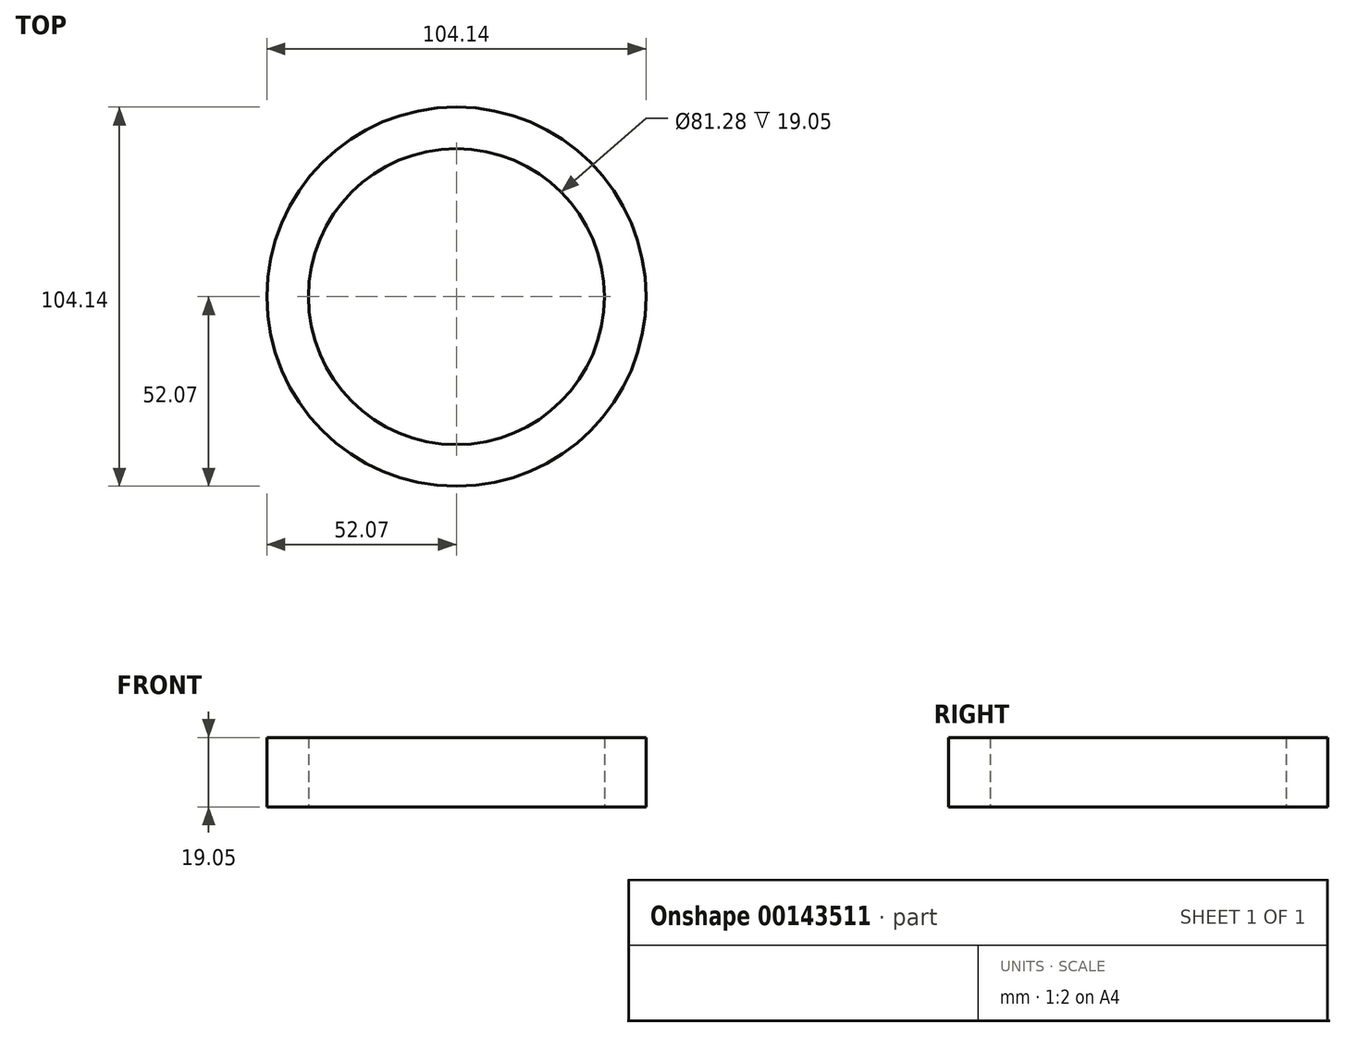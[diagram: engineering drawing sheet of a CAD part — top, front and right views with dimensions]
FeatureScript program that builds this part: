
annotation { "Feature Type Name" : "Feature", "Feature Type Description" : "" }
export const myFeature = defineFeature(function(context is Context, id is Id, definition is map)
    precondition{}
    {
        {
            var Q0;
            Q0=qCreatedBy(makeId("Top.planeOp"),FACE);
            var sketch = newSketch(context, id + "F0", { "sketchPlane" : qUnion([Q0])});
            skCircle(sketch, "E0", {"center": v(0, 0) * mm, "radius": 40.64 * mm});
            skSolve(sketch);
        }
        {
            var Q0;
            Q0=qCreatedBy(makeId("Top.planeOp"),FACE);
            var sketch = newSketch(context, id + "F1", { "sketchPlane" : qUnion([Q0])});
            skCircle(sketch, "E1", {"center": v(0, 0) * mm, "radius": 52.07 * mm});
            skSolve(sketch);
        }
        {
            var Q0;
            Q0=makeQuery(id+"F1.imprint","IMPRINT",FACE,{"disambiguationData":[TD([[makeQuery(id+"F1.imprint","IMPRINT",EDGE,{"derivedFrom":sQuery(id+"F1.wireOp",EDGE,"E1")}),1.0]])]});
            extrude(context, id + "F2", {"entities" : qUnion([Q0]), "depth" : 19.05 * mm});
        }
        {
            var Q0;
            Q0=makeQuery(id+"F0.imprint","IMPRINT",FACE,{"disambiguationData":[TD([[makeQuery(id+"F0.imprint","IMPRINT",EDGE,{"derivedFrom":sQuery(id+"F0.wireOp",EDGE,"E0")}),1.0]])]});
            extrude(context, id + "F3", {"entities" : qUnion([Q0]), "operationType" : NewBodyOperationType.REMOVE, "depth" : 19.05 * mm});
        }
    });
